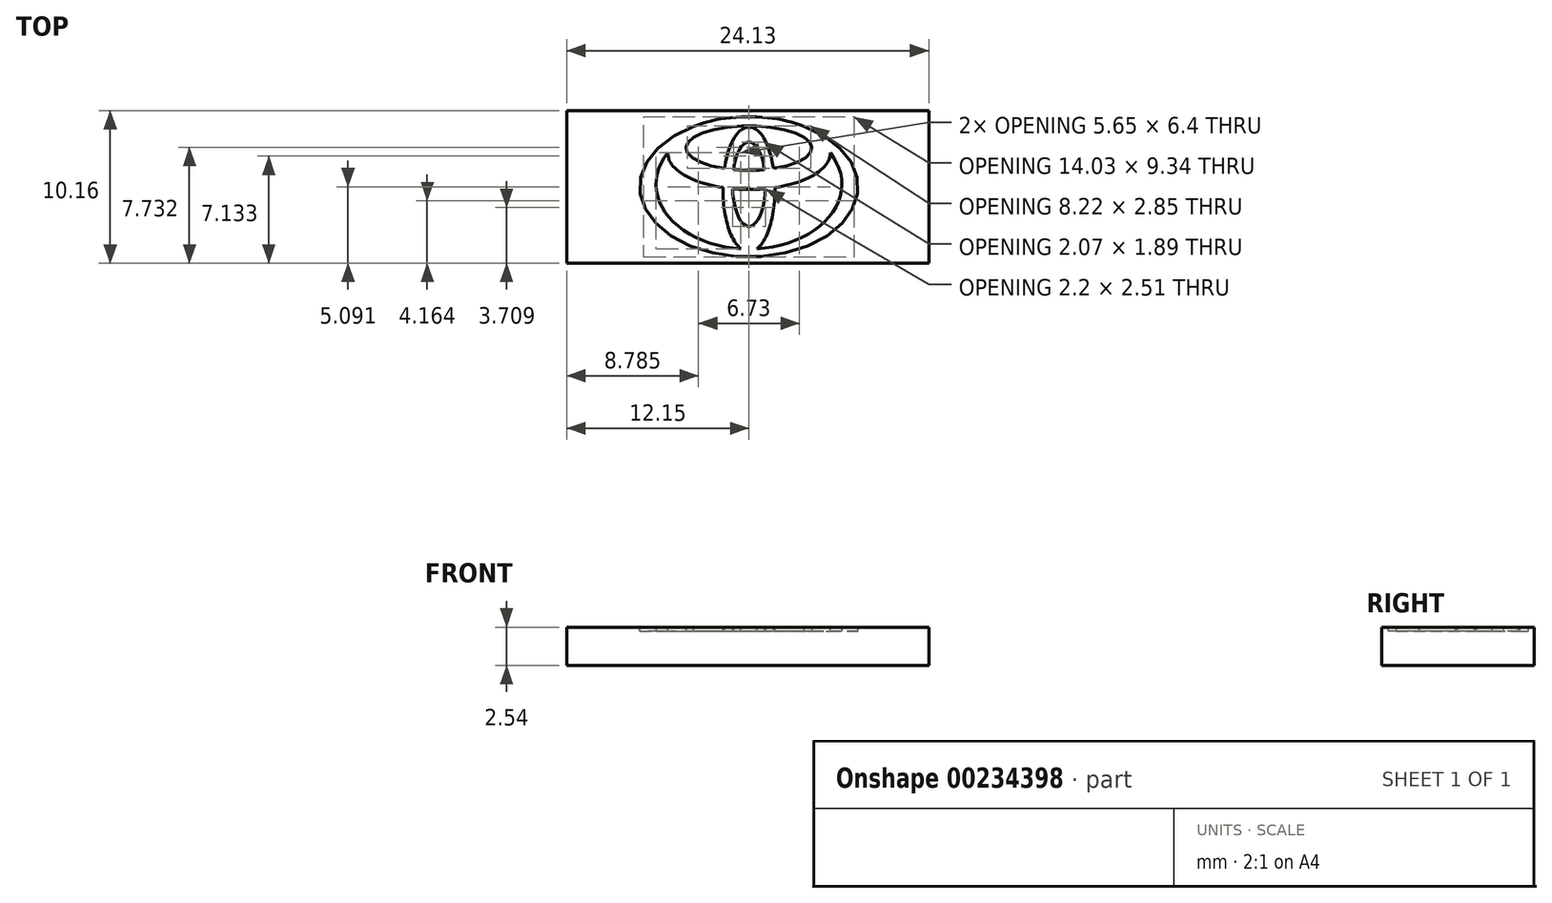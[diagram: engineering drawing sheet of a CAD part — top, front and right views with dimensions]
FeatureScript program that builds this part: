
annotation { "Feature Type Name" : "Feature", "Feature Type Description" : "" }
export const myFeature = defineFeature(function(context is Context, id is Id, definition is map)
    precondition{}
    {
        {
            var Q0;
            Q0=qCreatedBy(makeId("Top.planeOp"),FACE);
            var sketch = newSketch(context, id + "F0", { "sketchPlane" : qUnion([Q0])});
            skLineSegment(sketch, "E0.left", {"start": v(0, 0) * mm, "end": v(0, 0) * mm});
            skLineSegment(sketch, "E1.bottom", {"start": v(0, 0) * mm, "end": v(24.13, 0) * mm});
            skLineSegment(sketch, "E1.top", {"start": v(0, -10.16) * mm, "end": v(24.13, -10.16) * mm});
            skLineSegment(sketch, "E1.left", {"start": v(0, 0) * mm, "end": v(0, -10.16) * mm});
            skLineSegment(sketch, "E1.right", {"start": v(24.13, 0) * mm, "end": v(24.13, -10.16) * mm});
            skSolve(sketch);
        }
        {
            var Q0;
            Q0=qCreatedBy(makeId("Top.planeOp"),FACE);
            var sketch = newSketch(context, id + "F1", { "sketchPlane" : qUnion([Q0])});
            skLineSegment(sketch, "E2", {"start": v(10.42, -5.12) * mm, "end": v(10.42, -5.12) * mm});
            skEllipticalArc(sketch, "E3", {});
            skEllipticalArc(sketch, "E4", {});
            skLineSegment(sketch, "E5", {"start": v(10.51, -3.86) * mm, "end": v(10.51, -3.86) * mm});
            skEllipticalArc(sketch, "E6", {});
            skEllipticalArc(sketch, "E7", {});
            skEllipticalArc(sketch, "E8", {});
            skEllipticalArc(sketch, "E9", {});
            skEllipticalArc(sketch, "E10", {});
            skEllipticalArc(sketch, "E11", {});
            skEllipticalArc(sketch, "E12", {});
            skEllipticalArc(sketch, "E13", {});
            skLineSegment(sketch, "E14", {"start": v(12.69, -9.2) * mm, "end": v(12.69, -9.2) * mm});
            skEllipticalArc(sketch, "E15", {});
            skEllipticalArc(sketch, "E16", {});
            skEllipticalArc(sketch, "E17", {});
            skEllipticalArc(sketch, "E18", {});
            const initialGuessF1  = {"E3": [0.012149789370596409, -0.004892725708600156, 0, -1, 0.00281244736057402, 0.001104592944550833, 4.820465458971491, 1.4627198482080952], "E4": [0.012149789370596409, -0.004892725708600156, 0, -1, 0.00281244736057402, 0.001104592944550833, 1.9213345943509372, 4.361850712828648], "E6": [0.012149789370596409, -0.0024871101748786275, 1, 0, 0.004192138095141523, 0.0014860330821086791, 4.462322782180647, 4.9624551785887325], "E7": [0.012149789370596409, -0.0024871101748786275, 1, 0, 0.004192138095141523, 0.0014860330821086791, 5.1130588481775225, 4.311719112591857], "E8": [0.012149789370596409, -0.00282318894666517, 1, 0, 0.00541263467583855, 0.0024233037974880156, 5.038559015998256, 0.011771377894176966], "E9": [0.012149789370596409, -0.00282318894666517, 1, 0, 0.00541263467583855, 0.0024233037974880156, 4.5080845994429515, 4.916693361326428], "E10": [0.012149789370596409, -0.005246492744153185, 0, 1, 0.0041567619526573915, 0.0017351218878806415, 1.5400547915653744, 2.8455096107680653], "E11": [0.012149789370596409, -0.004892725708600156, 1, 0, 0.006190922682122202, 0.004321259153356856, 2.6346337173855017, 4.625208414431227], "E12": [0.012149789370596409, -0.005071165263760912, 1, 0, 0.0072717156213315225, 0.004666550107905985, 1.0395364465999162, 2.1020562069898765], "E13": [0.012149789370596409, -0.005071165263760912, 1, 0, 0.0072717156213315225, 0.004666550107905985, 2.1020562069898765, 1.0395364465999162], "E15": [0.012149789370596409, -0.004892725708600156, 1, 0, 0.006190922682122202, 0.004321259153356856, 4.799569546338152, 0.5069589362042914], "E16": [0.012149789370596409, -0.005246492744153185, 0, 1, 0.0041567619526573915, 0.0017351218878806415, 3.457487082237412, 1.2295668693740716], "E17": [0.012149789370596409, -0.00282318894666517, 1, 0, 0.00541263467583855, 0.0024233037974880156, 0.822175419194837, 2.3194172343949573], "E18": [0.012149789370596409, -0.00282318894666517, 1, 0, 0.00541263467583855, 0.0024233037974880156, 3.1298212756956163, 4.386218944771121]};
            skSetInitialGuess(sketch, initialGuessF1);
            skSolve(sketch);
        }
        {
            var Q0;
            Q0 = qSketchRegion(id + "F0", true);
            extrude(context, id + "F2", {"entities" : qUnion([Q0]), "oppositeDirection" : true, "depth" : 2.54 * mm});
        }
        {
            var Q0;
            Q0 = qSketchRegion(id + "F1", true);
            extrude(context, id + "F3", {"entities" : qUnion([Q0]), "operationType" : NewBodyOperationType.REMOVE, "oppositeDirection" : true, "depth" : 0.25 * mm});
        }
    });
